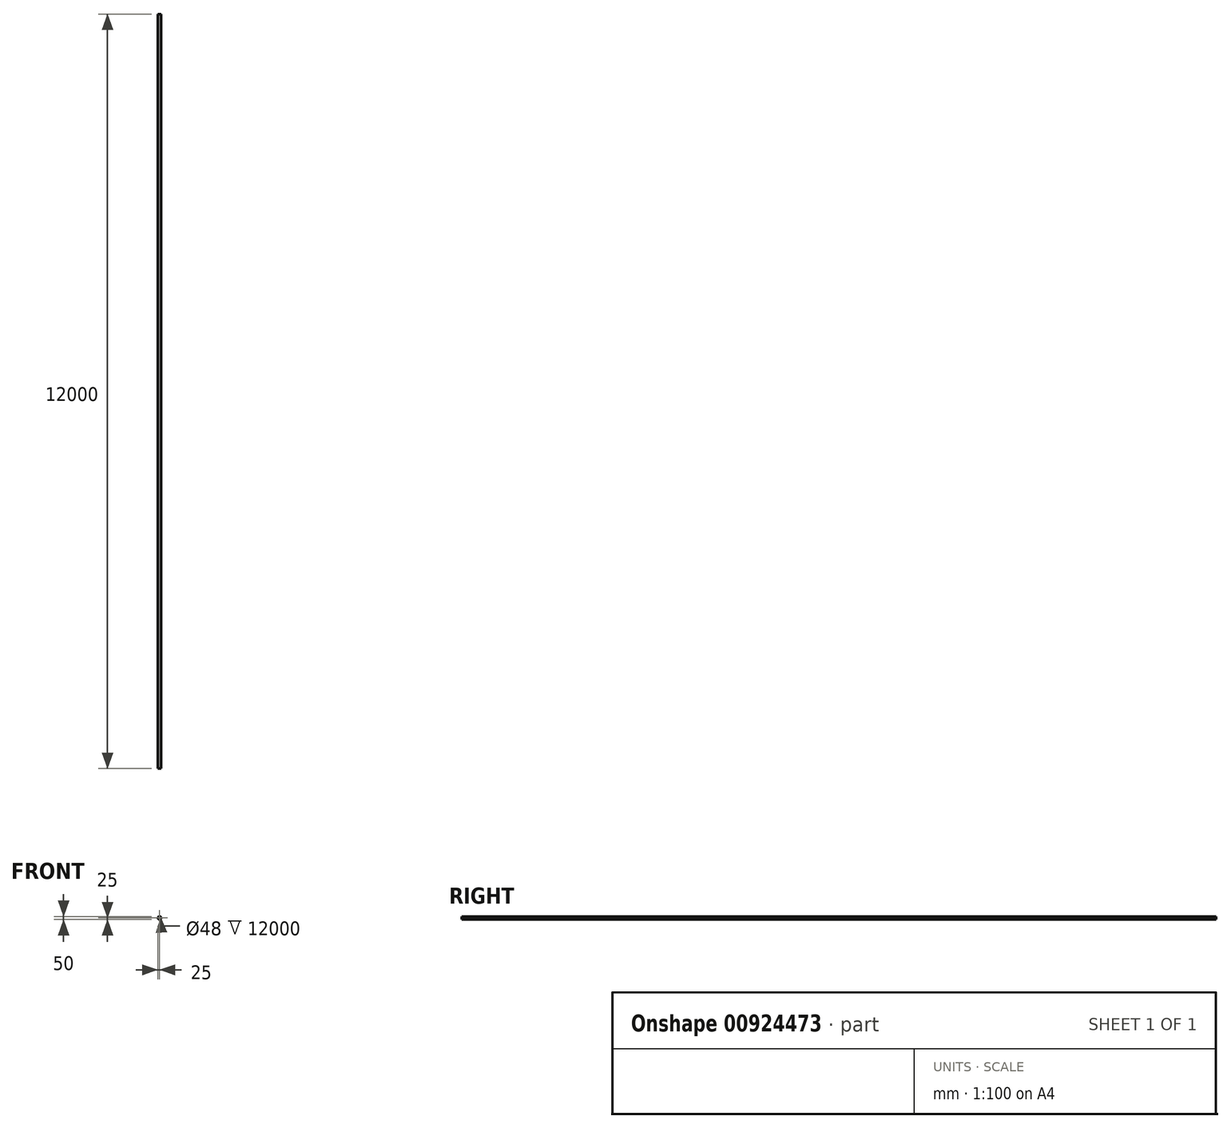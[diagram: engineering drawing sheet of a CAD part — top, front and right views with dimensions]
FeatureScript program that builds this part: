
annotation { "Feature Type Name" : "Feature", "Feature Type Description" : "" }
export const myFeature = defineFeature(function(context is Context, id is Id, definition is map)
    precondition{}
    {
        {
            var Q0;
            Q0=qCreatedBy(makeId("Front.planeOp"),FACE);
            var sketch = newSketch(context, id + "F0", { "sketchPlane" : qUnion([Q0])});
            skCircle(sketch, "E0", {"center": v(0, 0) * mm, "radius": 25 * mm});
            skCircle(sketch, "E1", {"center": v(0, 0) * mm, "radius": 24 * mm});
            skSolve(sketch);
        }
        {
            var Q0;
            Q0=makeQuery(id+"F0.imprint","IMPRINT",FACE,{"disambiguationData":[TD([[makeQuery(id+"F0.imprint","IMPRINT",EDGE,{"derivedFrom":sQuery(id+"F0.wireOp",EDGE,"E0")}),1.0]])]});
            extrude(context, id + "F1", {"entities" : qUnion([Q0]), "depth" : 12000 * mm, "offsetDistance" : 25 * mm});
        }
    });
